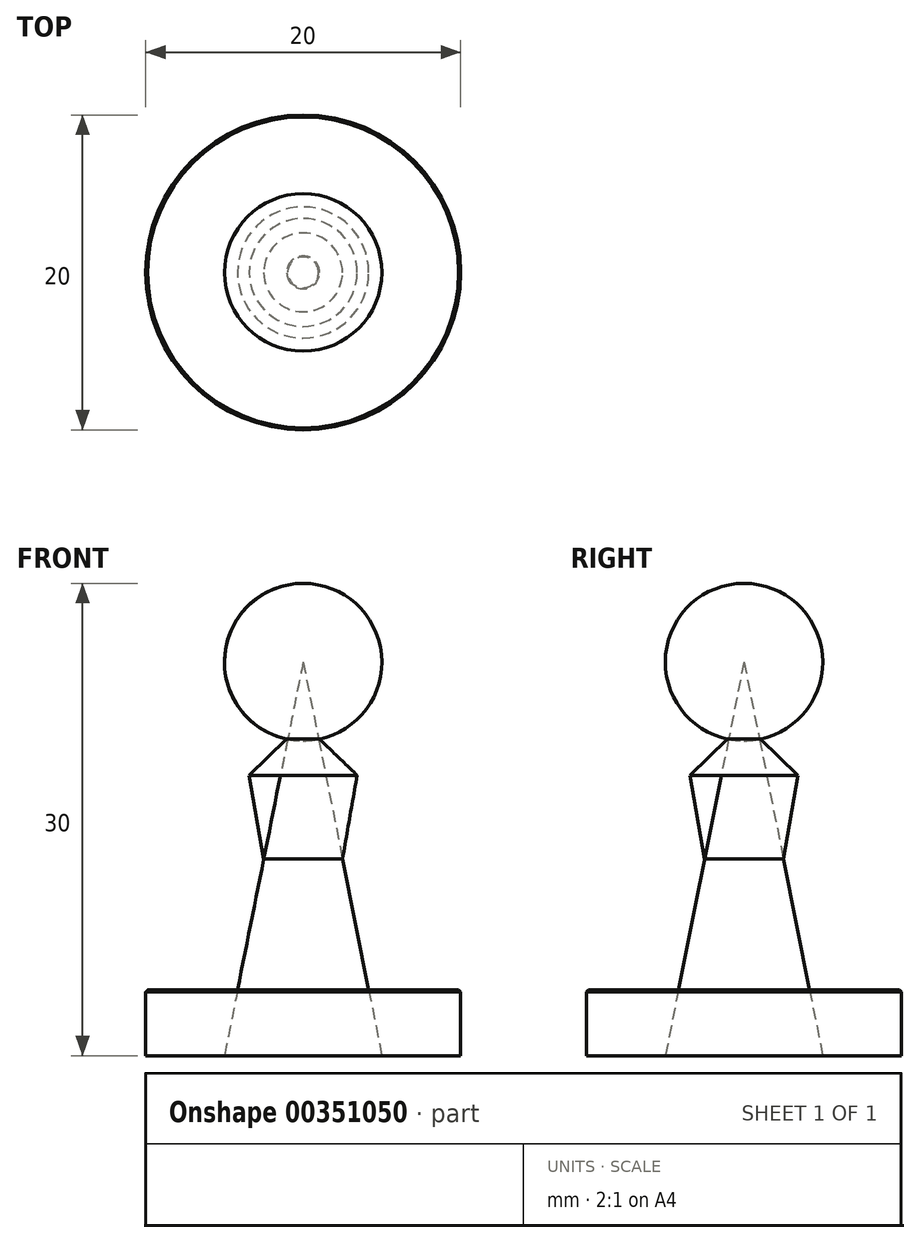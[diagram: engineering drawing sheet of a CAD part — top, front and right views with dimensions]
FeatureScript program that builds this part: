
annotation { "Feature Type Name" : "Feature", "Feature Type Description" : "" }
export const myFeature = defineFeature(function(context is Context, id is Id, definition is map)
    precondition{}
    {
        {
            assignVariable(context, id + "F0", {"name" : "W", "anyValue" : .5});
        }
        {
            var Q0;
            Q0=qCreatedBy(makeId("Front.planeOp"),FACE);
            var sketch = newSketch(context, id + "F1", { "sketchPlane" : qUnion([Q0])});
            skLineSegment(sketch, "E0", {"start": v(0, 0) * mm, "end": v(0, 30) * mm});
            skPoint(sketch, "E1", {"position": v(0, 20) * mm});
            skPoint(sketch, "E2", {"position": v(0, 25) * mm});
            skCircle(sketch, "E3", {"center": v(0, 25) * mm, "radius": 5 * mm});
            skLineSegment(sketch, "E4", {"start": v(0, 0) * mm, "end": v(-5, 0) * mm});
            skLineSegment(sketch, "E5", {"start": v(0, 25) * mm, "end": v(-5, 0) * mm});
            skLineSegment(sketch, "E6.bottom", {"start": v(0, 0) * mm, "end": v(-10, 0) * mm});
            skLineSegment(sketch, "E6.top", {"start": v(0, 4.17) * mm, "end": v(-10, 4.17) * mm});
            skLineSegment(sketch, "E6.left", {"start": v(0, 0) * mm, "end": v(0, 4.17) * mm});
            skLineSegment(sketch, "E6.right", {"start": v(-10, 0) * mm, "end": v(-10, 4.17) * mm});
            skLineSegment(sketch, "E7", {"start": v(-4.21, 22.3) * mm, "end": v(-2.5, 12.5) * mm});
            skSolve(sketch);
        }
        {
            var Q0;
            {var subQ0=sQuery(id+"F1.wireOp",EDGE,"E3");var subQ1=sQuery(id+"F1.wireOp",EDGE,"E0");var subQ2=makeQuery(id+"F1.imprint","INTERSECT",VERTEX,{"disambiguationData":[OD(0.0)],"derivedFrom":[subQ1,subQ0]});Q0=makeQuery(id+"F1.imprint","IMPRINT",FACE,{"disambiguationData":[TD([[makeQuery(id+"F1.imprint","IMPRINT",EDGE,{"disambiguationData":[TD([[subQ2,1.0]])],"derivedFrom":subQ1}),1.0]])]});}
            var Q1;
            {var subQ0=sQuery(id+"F1.wireOp",EDGE,"E5");var subQ1=sQuery(id+"F1.wireOp",EDGE,"E0");var subQ2=makeQuery(id+"F1.imprint","INTERSECT",VERTEX,{"derivedFrom":[subQ1,subQ0]});Q1=makeQuery(id+"F1.imprint","IMPRINT",FACE,{"disambiguationData":[TD([[makeQuery(id+"F1.imprint","IMPRINT",EDGE,{"disambiguationData":[TD([[subQ2,1.0]])],"derivedFrom":subQ1}),1.0]])]});}
            var Q2;
            {var subQ1=sQuery(id+"F1.wireOp",EDGE,"E0");var subQ3=sQuery(id+"F1.wireOp",EDGE,"E3");var subQ4=makeQuery(id+"F1.imprint","INTERSECT",VERTEX,{"disambiguationData":[OD(1.0)],"derivedFrom":[subQ1,subQ3]});Q2=makeQuery(id+"F1.imprint","IMPRINT",FACE,{"disambiguationData":[TD([[makeQuery(id+"F1.imprint","IMPRINT",EDGE,{"disambiguationData":[TD([[subQ4,1.0]])],"derivedFrom":subQ3}),-1.0]])]});}
            var Q3;
            {var subQ5=sQuery(id+"F1.wireOp",EDGE,"E6.left");Q3=makeQuery(id+"F1.imprint","IMPRINT",FACE,{"disambiguationData":[TD([[makeQuery(id+"F1.imprint","IMPRINT",EDGE,{"derivedFrom":subQ5}),1.0]])]});}
            var Q4;
            {var subQ5=sQuery(id+"F1.wireOp",EDGE,"E6.right");Q4=makeQuery(id+"F1.imprint","IMPRINT",FACE,{"disambiguationData":[TD([[makeQuery(id+"F1.imprint","IMPRINT",EDGE,{"derivedFrom":subQ5}),-1.0]])]});}
            var Q5;
            {var subQ0=sQuery(id+"F1.wireOp",EDGE,"E7");Q5=makeQuery(id+"F1.imprint","IMPRINT",FACE,{"disambiguationData":[TD([[makeQuery(id+"F1.imprint","IMPRINT",EDGE,{"derivedFrom":subQ0}),1.0]])]});}
            var Q6;
            Q6=sQuery(id+"F1.wireOp",EDGE,"E0");
            revolve(context, id + "F2", {"entities" : qUnion([Q0, Q1, Q2, Q3, Q4, Q5]), "axis" : qUnion([Q6]), "revolveType" : RevolveType.FULL});
        }
        {
            var Q0;
            Q0=makeQuery(id+"F2.opRevolve","SWEPT_EDGE",EDGE,{"disambiguationData":[OSD([sQuery(id+"F1.wireOp",EDGE,"E6.top"),sQuery(id+"F1.wireOp",EDGE,"E6.right")])]});
            chamfer(context, id + "F3", {"entities" : qUnion([Q0]), "width" : (getVariable(context, 'W') / 4) * mm, "tangentPropagation" : true});
        }
        {
            var Q0;
            Q0=makeQuery(id+"F2.opRevolve","SWEPT_EDGE",EDGE,{"disambiguationData":[OSD([sQuery(id+"F1.wireOp",EDGE,"E3"),sQuery(id+"F1.wireOp",EDGE,"E7")])]});
            chamfer(context, id + "F4", {"entities" : qUnion([Q0]), "width" : 2 * mm, "tangentPropagation" : true});
        }
    });
